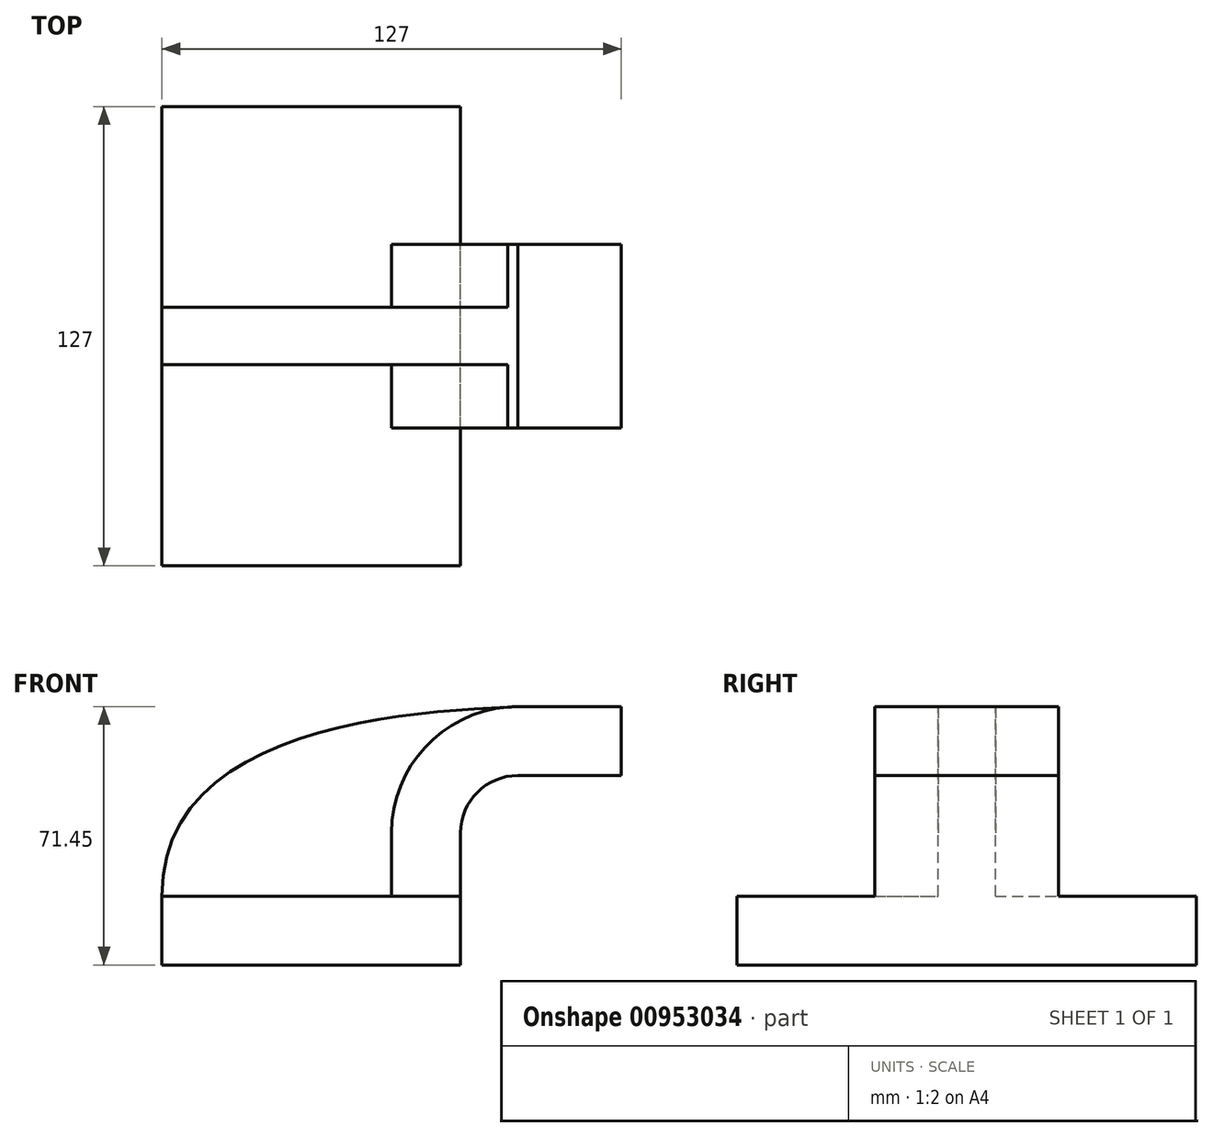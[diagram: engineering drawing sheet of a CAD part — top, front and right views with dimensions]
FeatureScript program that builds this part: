
annotation { "Feature Type Name" : "Feature", "Feature Type Description" : "" }
export const myFeature = defineFeature(function(context is Context, id is Id, definition is map)
    precondition{}
    {
        {
            var Q0;
            Q0=qCreatedBy(makeId("Front.planeOp"),FACE);
            var sketch = newSketch(context, id + "F0", { "sketchPlane" : qUnion([Q0])});
            skLineSegment(sketch, "E0.bottom", {"start": v(-94.4, -22.22) * mm, "end": v(-11.84, -22.22) * mm});
            skLineSegment(sketch, "E0.top", {"start": v(-94.4, -41.27) * mm, "end": v(-11.84, -41.27) * mm});
            skLineSegment(sketch, "E0.left", {"start": v(-94.4, -22.22) * mm, "end": v(-94.4, -41.27) * mm});
            skLineSegment(sketch, "E0.right", {"start": v(-11.84, -22.22) * mm, "end": v(-11.84, -41.27) * mm});
            skPoint(sketch, "E0.middle", {"position": v(-53.12, -31.74) * mm});
            skLineSegment(sketch, "E1.bottom", {"start": v(7.2, 6.36) * mm, "end": v(58, 6.36) * mm});
            skLineSegment(sketch, "E1.top", {"start": v(7.2, 34.93) * mm, "end": v(58, 34.93) * mm});
            skLineSegment(sketch, "E1.left", {"start": v(7.2, 6.36) * mm, "end": v(7.2, 34.93) * mm});
            skLineSegment(sketch, "E1.right", {"start": v(58, 6.36) * mm, "end": v(58, 34.93) * mm});
            skPoint(sketch, "E1.middle", {"position": v(32.6, 20.65) * mm});
            skLineSegment(sketch, "E2", {"start": v(-11.84, -22.22) * mm, "end": v(-11.84, -4.74) * mm});
            skArc(sketch, "E3", {"start": v(-11.84, -4.74) * mm, "mid": v(-7.2, 6.48) * mm, "end": v(4.03, 11.13) * mm});
            skLineSegment(sketch, "E4", {"start": v(4.03, 11.13) * mm, "end": v(32.6, 11.13) * mm});
            skArc(sketch, "E5.0", {"start": v(-30.9, -4.74) * mm, "mid": v(-20.66, 19.95) * mm, "end": v(4.03, 30.18) * mm});
            skLineSegment(sketch, "E5.1", {"start": v(-30.9, -22.22) * mm, "end": v(-30.9, -4.74) * mm});
            skLineSegment(sketch, "E6", {"start": v(4.03, 30.18) * mm, "end": v(7.2, 30.18) * mm});
            skLineSegment(sketch, "E7", {"start": v(32.6, 6.36) * mm, "end": v(32.6, 34.93) * mm});
            skLineSegment(sketch, "E8", {"start": v(7.2, 30.18) * mm, "end": v(32.6, 30.18) * mm});
            skFitSpline(sketch, "E9", {"points": [v(-94.4, -22.22) * mm, v(4.03, 30.18) * mm], "startDerivative": vector(-0.46, 140.01) * mm, "endDerivative": vector(95.78, 3.76) * mm});
            skPoint(sketch, "E10.orphan", {"position": v(-5.7, 11.13) * mm});
            skSolve(sketch);
        }
        {
            var Q0;
            Q0=makeQuery(id+"F0.imprint","IMPRINT",FACE,{"disambiguationData":[TD([[makeQuery(id+"F0.imprint","IMPRINT",EDGE,{"derivedFrom":sQuery(id+"F0.wireOp",EDGE,"E0.top")}),1.0]])]});
            extrude(context, id + "F1", {"entities" : qUnion([Q0]), "endBound" : BoundingType.SYMMETRIC, "depth" : 127 * mm, "offsetDistance" : 25.4 * mm});
        }
        {
            var Q0;
            {var subQ1=sQuery(id+"F0.wireOp",EDGE,"E2");Q0=makeQuery(id+"F0.imprint","IMPRINT",FACE,{"disambiguationData":[TD([[makeQuery(id+"F0.imprint","IMPRINT",EDGE,{"derivedFrom":subQ1}),1.0]])]});}
            var Q1;
            {var subQ0=sQuery(id+"F0.wireOp",EDGE,"E8");Q1=makeQuery(id+"F0.imprint","IMPRINT",FACE,{"disambiguationData":[TD([[makeQuery(id+"F0.imprint","IMPRINT",EDGE,{"derivedFrom":subQ0}),-1.0]])]});}
            extrude(context, id + "F2", {"entities" : qUnion([Q0, Q1]), "operationType" : NewBodyOperationType.ADD, "endBound" : BoundingType.SYMMETRIC, "depth" : 50.8 * mm, "offsetDistance" : 25.4 * mm});
        }
        {
            var Q0;
            {var subQ3=sQuery(id+"F0.wireOp",EDGE,"E5.1");Q0=makeQuery(id+"F0.imprint","IMPRINT",FACE,{"disambiguationData":[TD([[makeQuery(id+"F0.imprint","IMPRINT",EDGE,{"derivedFrom":subQ3}),1.0]])]});}
            extrude(context, id + "F3", {"entities" : qUnion([Q0]), "operationType" : NewBodyOperationType.ADD, "endBound" : BoundingType.SYMMETRIC, "depth" : 15.88 * mm, "offsetDistance" : 25.4 * mm});
        }
    });
